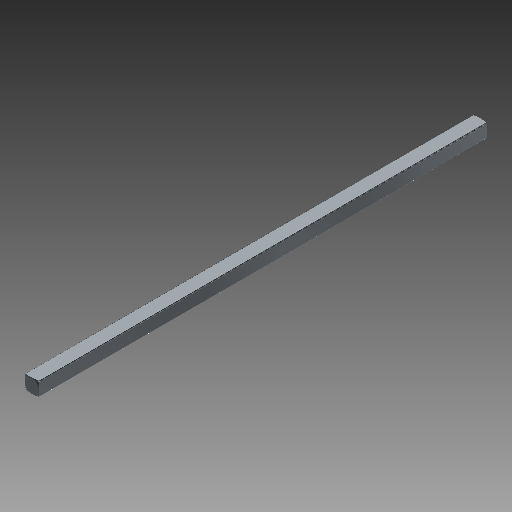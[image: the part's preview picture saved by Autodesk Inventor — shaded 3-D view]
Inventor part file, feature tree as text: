
AUTODESK INVENTOR PART (.ipt)
format: ipt  version: 2018 (Build 220112000, 112)  size: 167,936 bytes
history: native  units: in
note: dims shown in document units (in); Inventor stores cm internally (conversion verified against a paired STEP export)
features: sketch x2, plane x2, extrude x1, revolve x1, mirror x1, other x1
ambient origin geometry x8: Origin, YZ Plane, XZ Plane, XY Plane, X Axis, Y Axis, Z Axis, Center Point
bodies: Solid1 (feature_tree)
feature tree (8):
  sketch  "Sketch1"  dims[d0=4.0in d1=0.0in d2=90.0deg]
  extrude  "Extrusion1"  TaperAngle=90.0deg  [1 undecoded]
  plane  "Work Plane1"
  revolve  "Revolution1"  [1 undecoded]
  plane  "Work Plane2"
  mirror  "Mirror1"
  other  "Work Axis1"
  sketch  "Sketch2"  dims[d3=90.0deg]
note: 2 required parameter values undecoded (feature->parameter linkage not recoverable at this tier; creation-order binding heuristic only, values carry confidence <= 0.55)
